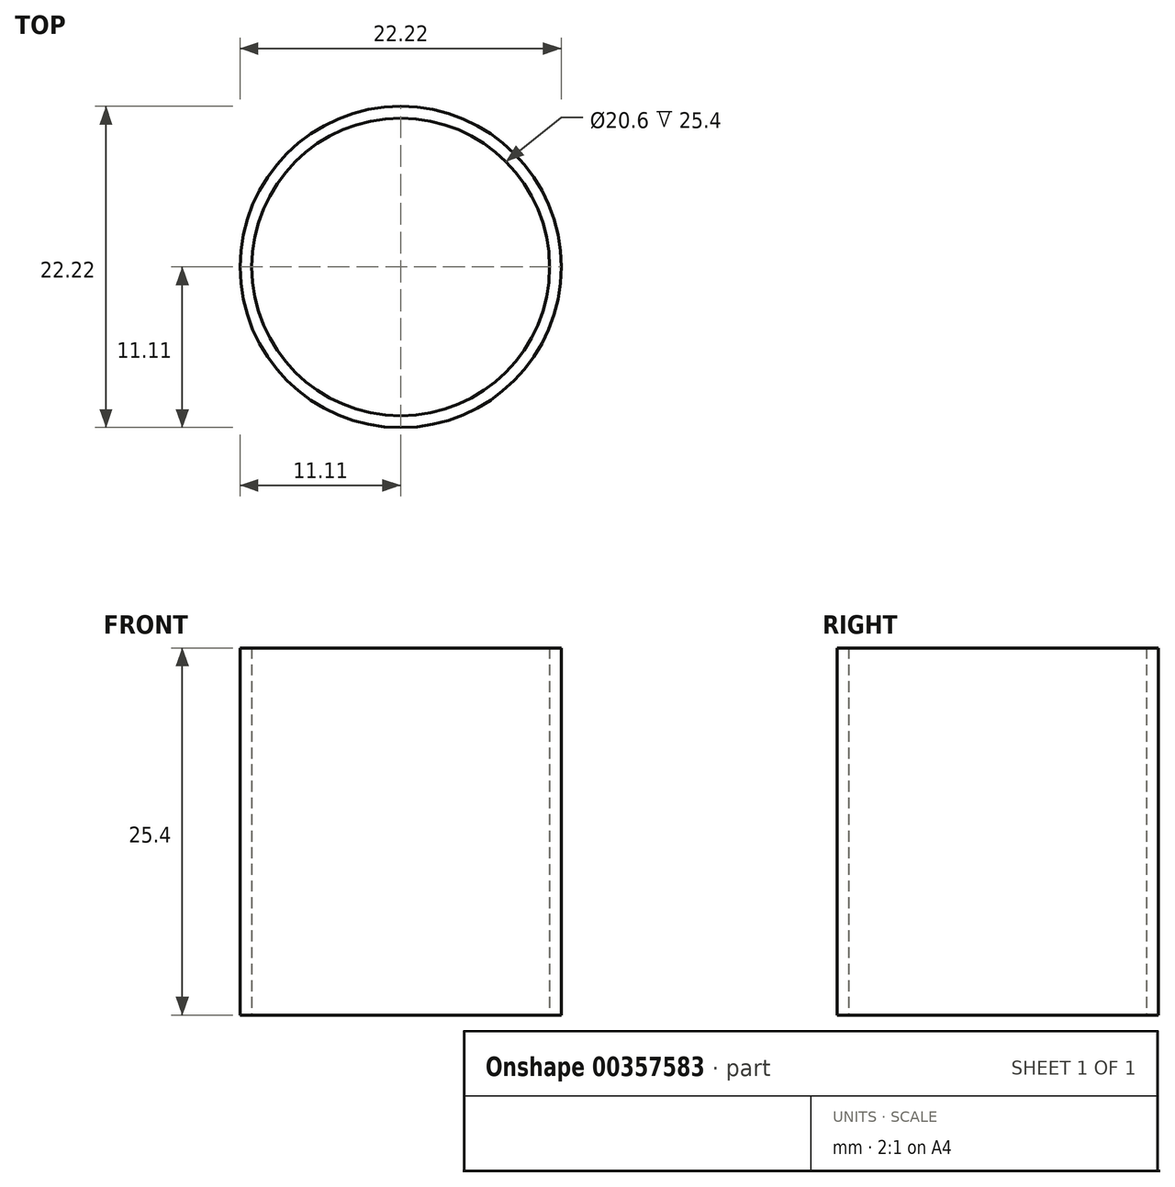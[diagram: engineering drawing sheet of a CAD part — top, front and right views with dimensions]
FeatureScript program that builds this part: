
annotation { "Feature Type Name" : "Feature", "Feature Type Description" : "" }
export const myFeature = defineFeature(function(context is Context, id is Id, definition is map)
    precondition{}
    {
        {
            var Q0;
            Q0=qCreatedBy(makeId("Top.planeOp"),FACE);
            var sketch = newSketch(context, id + "F0", { "sketchPlane" : qUnion([Q0])});
            skCircle(sketch, "E0", {"center": v(0, 0) * mm, "radius": 10.3 * mm});
            skCircle(sketch, "E1", {"center": v(0, 0) * mm, "radius": 11.11 * mm});
            skSolve(sketch);
        }
        {
            var Q0;
            Q0 = qSketchRegion(id + "F0", true);
            extrude(context, id + "F1", {"entities" : qUnion([Q0]), "offsetDistance" : 25.4 * mm, "depth" : 25.4 * mm});
        }
    });
